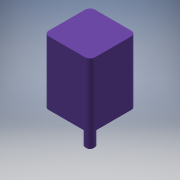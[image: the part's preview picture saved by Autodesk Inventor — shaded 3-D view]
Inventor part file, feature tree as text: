
AUTODESK INVENTOR PART (.ipt)
format: ipt  version: 2016 (Build 200138000, 138)  size: 121,344 bytes
history: native  units: mm
features: reference x5, extrude x3, sketch x3, hole x1, chamfer x1, fillet x1
ambient origin geometry x8: Origin, YZ Plane, XZ Plane, XY Plane, X Axis, Y Axis, Z Axis, Center Point
bodies: Solid1 (feature_tree)
feature tree (14):
  extrude  "Extrusion1"  Depth=20.32mm
  hole  "Hole1"  [1 undecoded]
  sketch  "Sketch3"  dims[d5=3.0mm d6=6.0mm d7=4.0mm d8=2.0mm d9=90.0deg d10=8.0mm d11=20.594885mm d12=1.5mm d13=0.0mm d14=4.0mm d15=15.0mm d16=0.0mm d17=0.6mm d18=2.0mm d19=45.0deg d20=2.16mm]
  extrude  "Extrusion2"  Depth=1.5mm TaperAngle=0.0deg
  extrude  "Extrusion3"  Depth=2.16mm
  chamfer  "Chamfer1"  Distance=15.0mm
  fillet  "Fillet1"  Radius=2.0mm
  sketch  "Sketch1"  dims[d0=20.32mm d1=20.32mm]
  reference  "Reference1"
  reference  "Reference2"
  reference  "Reference3"
  reference  "Reference4"
  reference  "Reference5"
  sketch  "Sketch2"  dims[d2=14.99mm d3=28.0mm d4=0.0mm]
note: 1 required parameter value undecoded (feature->parameter linkage not recoverable at this tier; creation-order binding heuristic only, values carry confidence <= 0.55)
